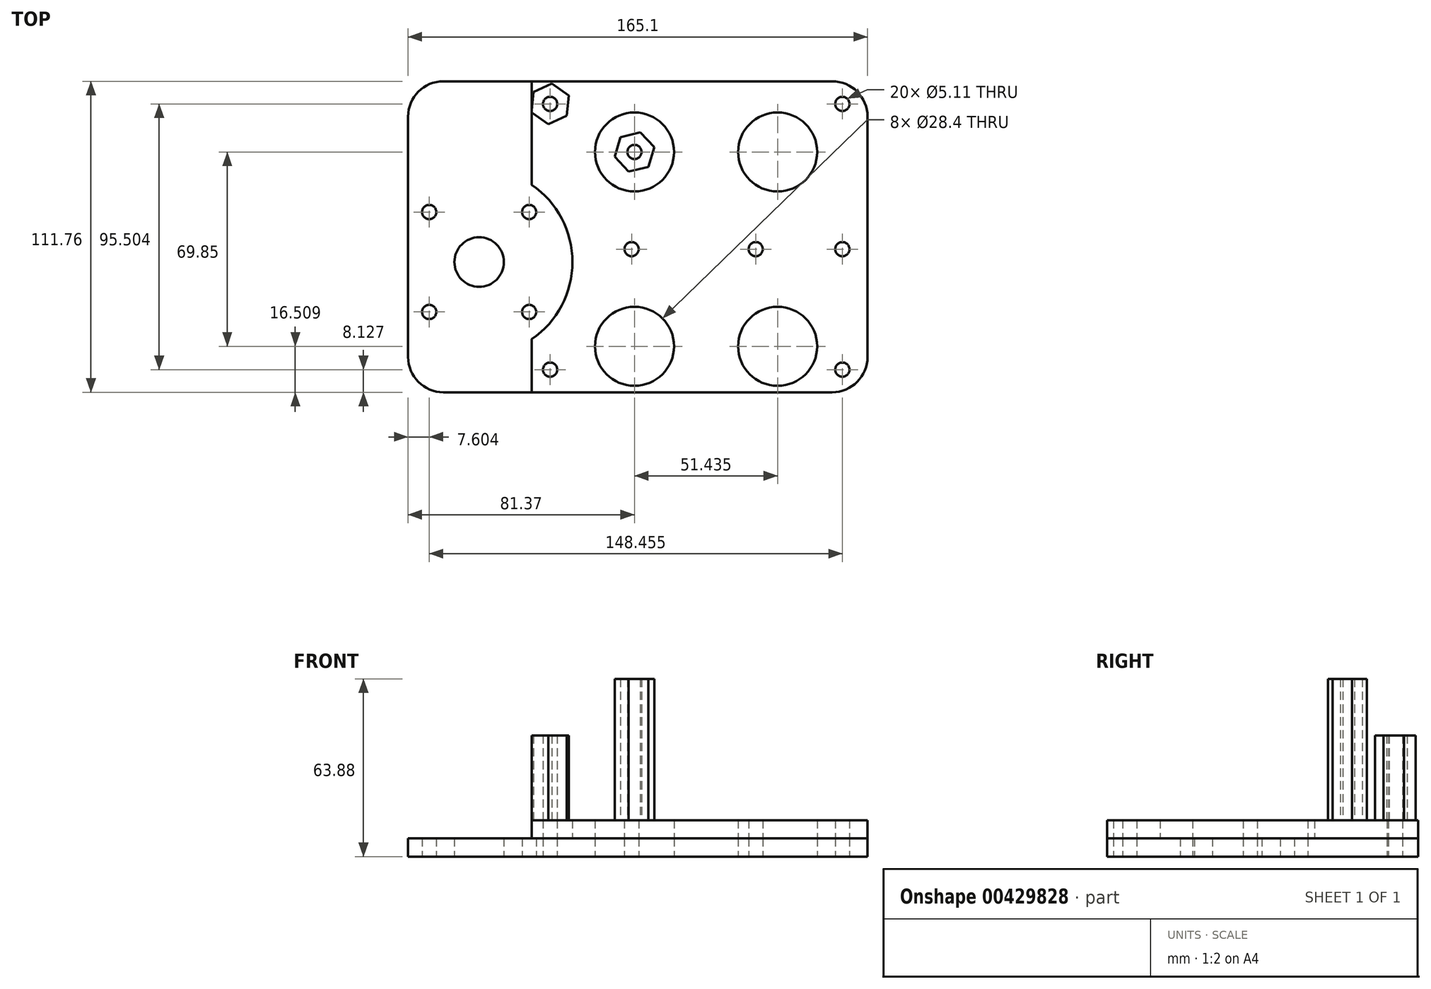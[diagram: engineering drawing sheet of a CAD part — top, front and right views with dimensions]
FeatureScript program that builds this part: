
annotation { "Feature Type Name" : "Feature", "Feature Type Description" : "" }
export const myFeature = defineFeature(function(context is Context, id is Id, definition is map)
    precondition{}
    {
        {
            var Q0;
            Q0=qCreatedBy(makeId("Top.planeOp"),FACE);
            var sketch = newSketch(context, id + "F0", { "sketchPlane" : qUnion([Q0])});
            skLineSegment(sketch, "E0.bottom", {"start": v(-81.37, 110.22) * mm, "end": v(83.73, 110.22) * mm});
            skLineSegment(sketch, "E0.top", {"start": v(-81.37, -1.54) * mm, "end": v(83.73, -1.54) * mm});
            skLineSegment(sketch, "E0.left", {"start": v(-81.37, 110.22) * mm, "end": v(-81.37, -1.54) * mm});
            skLineSegment(sketch, "E0.right", {"start": v(83.73, 110.22) * mm, "end": v(83.73, -1.54) * mm});
            skPoint(sketch, "E0.middle", {"position": v(1.18, 54.34) * mm});
            skLineSegment(sketch, "E1", {"start": v(25.72, 110.22) * mm, "end": v(25.72, -1.54) * mm, "construction": true});
            skCircle(sketch, "E2", {"center": v(0, 84.82) * mm, "radius": 14.2 * mm});
            skCircle(sketch, "E3", {"center": v(51.44, 84.82) * mm, "radius": 14.2 * mm});
            skLineSegment(sketch, "E4.trimOffspring", {"start": v(0, 84.82) * mm, "end": v(51.44, 84.82) * mm, "construction": true});
            skPoint(sketch, "E5.trimOffspring.end.orphan", {"position": v(83.73, 92.44) * mm});
            skPoint(sketch, "E6", {"position": v(25.72, 84.82) * mm});
            skCircle(sketch, "E7", {"center": v(0, 84.82) * mm, "radius": 25.4 * mm, "construction": true});
            skCircle(sketch, "E8", {"center": v(51.44, 84.82) * mm, "radius": 25.4 * mm, "construction": true});
            skLineSegment(sketch, "E9", {"start": v(-21.94, 49.9) * mm, "end": v(65.42, 49.9) * mm, "construction": true});
            skCircle(sketch, "E10.MirrorC", {"center": v(0, 14.97) * mm, "radius": 25.4 * mm, "construction": true});
            skCircle(sketch, "E11.MirrorC", {"center": v(0, 14.97) * mm, "radius": 14.2 * mm});
            skCircle(sketch, "E12.MirrorC", {"center": v(51.44, 14.97) * mm, "radius": 14.2 * mm});
            skCircle(sketch, "E13.MirrorC", {"center": v(51.44, 14.97) * mm, "radius": 25.4 * mm, "construction": true});
            skLineSegment(sketch, "E14.bottom", {"start": v(-73.77, 63.23) * mm, "end": v(-37.85, 63.23) * mm, "construction": true});
            skLineSegment(sketch, "E14.top", {"start": v(-73.77, 27.3) * mm, "end": v(-37.85, 27.3) * mm, "construction": true});
            skLineSegment(sketch, "E14.left", {"start": v(-73.77, 63.23) * mm, "end": v(-73.77, 27.3) * mm, "construction": true});
            skLineSegment(sketch, "E14.right", {"start": v(-37.85, 63.23) * mm, "end": v(-37.85, 27.3) * mm, "construction": true});
            skPoint(sketch, "E14.middle", {"position": v(-55.8, 45.27) * mm});
            skCircle(sketch, "E15", {"center": v(-55.8, 45.27) * mm, "radius": 8.9 * mm});
            skCircle(sketch, "E16", {"center": v(-73.77, 63.23) * mm, "radius": 2.55 * mm});
            skCircle(sketch, "E17", {"center": v(-37.85, 63.23) * mm, "radius": 2.55 * mm});
            skCircle(sketch, "E18", {"center": v(-37.85, 27.3) * mm, "radius": 2.55 * mm});
            skCircle(sketch, "E19", {"center": v(-73.77, 27.3) * mm, "radius": 2.55 * mm});
            skCircle(sketch, "E20", {"center": v(-55.8, 45.27) * mm, "radius": 25.4 * mm, "construction": true});
            skCircle(sketch, "E21", {"center": v(-1.05, 49.9) * mm, "radius": 2.55 * mm});
            skCircle(sketch, "E22", {"center": v(43.56, 49.9) * mm, "radius": 2.55 * mm});
            skCircle(sketch, "E23", {"center": v(74.69, 49.9) * mm, "radius": 2.55 * mm});
            skCircle(sketch, "E24", {"center": v(74.69, 6.59) * mm, "radius": 2.55 * mm});
            skCircle(sketch, "E25", {"center": v(74.69, 102.1) * mm, "radius": 2.55 * mm});
            skCircle(sketch, "E26", {"center": v(-30.32, 102.1) * mm, "radius": 2.55 * mm});
            skCircle(sketch, "E27", {"center": v(-30.32, 6.59) * mm, "radius": 2.55 * mm});
            skCircle(sketch, "E28", {"center": v(-30.32, 6.59) * mm, "radius": 6.88 * mm, "construction": true});
            skCircle(sketch, "E29", {"center": v(74.69, 6.59) * mm, "radius": 6.87 * mm, "construction": true});
            skLineSegment(sketch, "E30.bottom", {"start": v(-30.32, 102.1) * mm, "end": v(74.69, 102.1) * mm, "construction": true});
            skLineSegment(sketch, "E30.top", {"start": v(-30.32, 6.59) * mm, "end": v(74.69, 6.59) * mm, "construction": true});
            skLineSegment(sketch, "E30.left", {"start": v(-30.32, 102.1) * mm, "end": v(-30.32, 6.59) * mm, "construction": true});
            skLineSegment(sketch, "E30.right", {"start": v(74.69, 102.1) * mm, "end": v(74.69, 6.59) * mm, "construction": true});
            skSolve(sketch);
        }
        {
            var Q0;
            Q0=makeQuery(id+"F0.imprint","IMPRINT",FACE,{"disambiguationData":[TD([[makeQuery(id+"F0.imprint","IMPRINT",EDGE,{"derivedFrom":sQuery(id+"F0.wireOp",EDGE,"E0.bottom")}),-1.0]])]});
            extrude(context, id + "F1", {"entities" : qUnion([Q0]), "depth" : 6.6 * mm});
        }
        {
            var Q0;
            Q0=makeQuery(id+"F1.opExtrude","SWEPT_EDGE",EDGE,{"disambiguationData":[OSD([sQuery(id+"F0.wireOp",EDGE,"E0.bottom"),sQuery(id+"F0.wireOp",EDGE,"E0.left")])]});
            var Q1;
            Q1=makeQuery(id+"F1.opExtrude","SWEPT_EDGE",EDGE,{"disambiguationData":[OSD([sQuery(id+"F0.wireOp",EDGE,"E0.top"),sQuery(id+"F0.wireOp",EDGE,"E0.left")])]});
            var Q2;
            Q2=makeQuery(id+"F1.opExtrude","SWEPT_EDGE",EDGE,{"disambiguationData":[OSD([sQuery(id+"F0.wireOp",EDGE,"E0.top"),sQuery(id+"F0.wireOp",EDGE,"E0.right")])]});
            var Q3;
            Q3=makeQuery(id+"F1.opExtrude","SWEPT_EDGE",EDGE,{"disambiguationData":[OSD([sQuery(id+"F0.wireOp",EDGE,"E0.bottom"),sQuery(id+"F0.wireOp",EDGE,"E0.right")])]});
            fillet(context, id + "F2", {"entities" : qUnion([Q0, Q1, Q2, Q3]), "radius" : 12.7 * mm, "tangentPropagation" : true, "allowEdgeOverflow" : false});
        }
        {
            var Q0;
            Q0=makeQuery(id+"F1.opExtrude","CAP_FACE",FACE,{"disambiguationData":[OSD([sQuery(id+"F0.wireOp",EDGE,"E0.bottom"),sQuery(id+"F0.wireOp",EDGE,"E0.top"),sQuery(id+"F0.wireOp",EDGE,"E0.left"),sQuery(id+"F0.wireOp",EDGE,"E0.right"),sQuery(id+"F0.wireOp",EDGE,"E2"),sQuery(id+"F0.wireOp",EDGE,"E3"),sQuery(id+"F0.wireOp",EDGE,"E11.MirrorC"),sQuery(id+"F0.wireOp",EDGE,"E12.MirrorC"),sQuery(id+"F0.wireOp",EDGE,"E15"),sQuery(id+"F0.wireOp",EDGE,"E16"),sQuery(id+"F0.wireOp",EDGE,"E17"),sQuery(id+"F0.wireOp",EDGE,"E18"),sQuery(id+"F0.wireOp",EDGE,"E19"),sQuery(id+"F0.wireOp",EDGE,"E21"),sQuery(id+"F0.wireOp",EDGE,"E22"),sQuery(id+"F0.wireOp",EDGE,"E23"),sQuery(id+"F0.wireOp",EDGE,"E24"),sQuery(id+"F0.wireOp",EDGE,"E25"),sQuery(id+"F0.wireOp",EDGE,"E26"),sQuery(id+"F0.wireOp",EDGE,"E27")])],"isStart":false});
            var sketch = newSketch(context, id + "F3", { "sketchPlane" : qUnion([Q0])});
            skCircle(sketch, "E31.0", {"center": v(0, 84.82) * mm, "radius": 14.2 * mm});
            skCircle(sketch, "E32.0", {"center": v(-55.8, 45.27) * mm, "radius": 8.9 * mm});
            skCircle(sketch, "E33.0", {"center": v(0, 14.97) * mm, "radius": 14.2 * mm});
            skCircle(sketch, "E34.0", {"center": v(-30.32, 6.59) * mm, "radius": 2.55 * mm});
            skCircle(sketch, "E35.0", {"center": v(51.44, 14.97) * mm, "radius": 14.2 * mm});
            skCircle(sketch, "E36.0", {"center": v(51.44, 84.82) * mm, "radius": 14.2 * mm});
            skCircle(sketch, "E37.0", {"center": v(-30.32, 102.1) * mm, "radius": 2.55 * mm});
            skCircle(sketch, "E38.0", {"center": v(74.69, 102.1) * mm, "radius": 2.55 * mm});
            skCircle(sketch, "E39.0", {"center": v(74.69, 49.9) * mm, "radius": 2.55 * mm});
            skCircle(sketch, "E40.0", {"center": v(43.56, 49.9) * mm, "radius": 2.55 * mm});
            skCircle(sketch, "E41.0", {"center": v(-1.05, 49.9) * mm, "radius": 2.55 * mm});
            skCircle(sketch, "E42.0", {"center": v(-37.85, 27.3) * mm, "radius": 2.55 * mm});
            skCircle(sketch, "E43.0", {"center": v(-37.85, 63.23) * mm, "radius": 2.55 * mm});
            skCircle(sketch, "E44.0", {"center": v(-73.77, 27.3) * mm, "radius": 2.55 * mm});
            skCircle(sketch, "E45.0", {"center": v(-73.77, 63.23) * mm, "radius": 2.55 * mm});
            skLineSegment(sketch, "E46.0", {"start": v(-68.67, 110.22) * mm, "end": v(71.03, 110.22) * mm});
            skArc(sketch, "E47.0", {"start": v(-68.67, 110.22) * mm, "mid": v(-77.65, 106.5) * mm, "end": v(-81.37, 97.52) * mm});
            skLineSegment(sketch, "E48.0", {"start": v(-68.67, -1.54) * mm, "end": v(71.03, -1.54) * mm});
            skLineSegment(sketch, "E49.0", {"start": v(-81.37, 97.52) * mm, "end": v(-81.37, 11.16) * mm});
            skArc(sketch, "E50.0", {"start": v(-81.37, 11.16) * mm, "mid": v(-77.65, 2.18) * mm, "end": v(-68.67, -1.54) * mm});
            skArc(sketch, "E51.0", {"start": v(71.03, -1.54) * mm, "mid": v(80.01, 2.18) * mm, "end": v(83.73, 11.16) * mm});
            skLineSegment(sketch, "E52.0", {"start": v(83.73, 97.52) * mm, "end": v(83.73, 11.16) * mm});
            skArc(sketch, "E53.0", {"start": v(83.73, 97.52) * mm, "mid": v(80.01, 106.5) * mm, "end": v(71.03, 110.22) * mm});
            skArc(sketch, "E54", {"start": v(-36.92, 17.57) * mm, "mid": v(-22.28, 45.27) * mm, "end": v(-36.92, 72.97) * mm});
            skLineSegment(sketch, "E55", {"start": v(-36.92, 110.22) * mm, "end": v(-36.92, 72.97) * mm});
            skLineSegment(sketch, "E56.trimOffspring", {"start": v(-36.92, 17.57) * mm, "end": v(-36.92, -1.54) * mm});
            skSolve(sketch);
        }
        {
            var Q0;
            Q0=makeQuery(id+"F3.imprint","IMPRINT",FACE,{"disambiguationData":[TD([[makeQuery(id+"F3.imprint","IMPRINT",EDGE,{"derivedFrom":sQuery(id+"F3.wireOp",EDGE,"E31.0")}),-1.0]])]});
            extrude(context, id + "F4", {"entities" : qUnion([Q0]), "depth" : 6.48 * mm});
        }
        {
            var Q0;
            Q0=makeQuery(id+"F4.opExtrude","CAP_FACE",FACE,{"disambiguationData":[OSD([sQuery(id+"F0.wireOp",EDGE,"E24"),sQuery(id+"F3.wireOp",EDGE,"E31.0"),sQuery(id+"F3.wireOp",EDGE,"E33.0"),sQuery(id+"F3.wireOp",EDGE,"E34.0"),sQuery(id+"F3.wireOp",EDGE,"E35.0"),sQuery(id+"F3.wireOp",EDGE,"E36.0"),sQuery(id+"F3.wireOp",EDGE,"E37.0"),sQuery(id+"F3.wireOp",EDGE,"E38.0"),sQuery(id+"F3.wireOp",EDGE,"E39.0"),sQuery(id+"F3.wireOp",EDGE,"E40.0"),sQuery(id+"F3.wireOp",EDGE,"E41.0"),sQuery(id+"F3.wireOp",EDGE,"E46.0"),sQuery(id+"F3.wireOp",EDGE,"E48.0"),sQuery(id+"F3.wireOp",EDGE,"E51.0"),sQuery(id+"F3.wireOp",EDGE,"E52.0"),sQuery(id+"F3.wireOp",EDGE,"E53.0"),sQuery(id+"F3.wireOp",EDGE,"E54"),sQuery(id+"F3.wireOp",EDGE,"E55"),sQuery(id+"F3.wireOp",EDGE,"E56.trimOffspring")])],"isStart":false});
            var sketch = newSketch(context, id + "F5", { "sketchPlane" : qUnion([Q0])});
            skCircle(sketch, "E57.0", {"center": v(-30.32, 102.1) * mm, "radius": 2.55 * mm});
            skCircle(sketch, "E58.cCircle", {"center": v(-30.32, 102.1) * mm, "radius": 7.33 * mm, "construction": true});
            skLineSegment(sketch, "E58.0", {"start": v(-24.34, 97.85) * mm, "end": v(-31, 94.8) * mm});
            skLineSegment(sketch, "E58.1", {"start": v(-31, 94.8) * mm, "end": v(-36.98, 99.04) * mm});
            skLineSegment(sketch, "E58.2", {"start": v(-36.98, 99.04) * mm, "end": v(-36.3, 106.34) * mm});
            skLineSegment(sketch, "E58.3", {"start": v(-36.3, 106.34) * mm, "end": v(-29.63, 109.4) * mm});
            skLineSegment(sketch, "E58.4", {"start": v(-29.63, 109.4) * mm, "end": v(-23.65, 105.15) * mm});
            skLineSegment(sketch, "E58.5", {"start": v(-23.65, 105.15) * mm, "end": v(-24.34, 97.85) * mm});
            skSolve(sketch);
        }
        {
            var Q0;
            Q0=makeQuery(id+"F5.imprint","IMPRINT",FACE,{"disambiguationData":[TD([[makeQuery(id+"F5.imprint","IMPRINT",EDGE,{"derivedFrom":sQuery(id+"F5.wireOp",EDGE,"E57.0")}),-1.0]])]});
            extrude(context, id + "F6", {"entities" : qUnion([Q0]), "depth" : 30.48 * mm});
        }
        {
            var Q0;
            Q0=makeQuery(id+"F4.opExtrude","CAP_FACE",FACE,{"disambiguationData":[OSD([sQuery(id+"F0.wireOp",EDGE,"E24"),sQuery(id+"F3.wireOp",EDGE,"E31.0"),sQuery(id+"F3.wireOp",EDGE,"E33.0"),sQuery(id+"F3.wireOp",EDGE,"E34.0"),sQuery(id+"F3.wireOp",EDGE,"E35.0"),sQuery(id+"F3.wireOp",EDGE,"E36.0"),sQuery(id+"F3.wireOp",EDGE,"E37.0"),sQuery(id+"F3.wireOp",EDGE,"E38.0"),sQuery(id+"F3.wireOp",EDGE,"E39.0"),sQuery(id+"F3.wireOp",EDGE,"E40.0"),sQuery(id+"F3.wireOp",EDGE,"E41.0"),sQuery(id+"F3.wireOp",EDGE,"E46.0"),sQuery(id+"F3.wireOp",EDGE,"E48.0"),sQuery(id+"F3.wireOp",EDGE,"E51.0"),sQuery(id+"F3.wireOp",EDGE,"E52.0"),sQuery(id+"F3.wireOp",EDGE,"E53.0"),sQuery(id+"F3.wireOp",EDGE,"E54"),sQuery(id+"F3.wireOp",EDGE,"E55"),sQuery(id+"F3.wireOp",EDGE,"E56.trimOffspring")])],"isStart":false});
            var sketch = newSketch(context, id + "F7", { "sketchPlane" : qUnion([Q0])});
            skCircle(sketch, "E59.0", {"center": v(0, 84.82) * mm, "radius": 14.2 * mm});
            skCircle(sketch, "E60", {"center": v(0, 84.82) * mm, "radius": 2.55 * mm});
            skCircle(sketch, "E61.cCircle", {"center": v(0, 84.82) * mm, "radius": 7.33 * mm, "construction": true});
            skLineSegment(sketch, "E61.0", {"start": v(5.02, 79.48) * mm, "end": v(-2.12, 77.8) * mm});
            skLineSegment(sketch, "E61.1", {"start": v(-2.12, 77.8) * mm, "end": v(-7.14, 83.14) * mm});
            skLineSegment(sketch, "E61.2", {"start": v(-7.14, 83.14) * mm, "end": v(-5.02, 90.16) * mm});
            skLineSegment(sketch, "E61.3", {"start": v(-5.02, 90.16) * mm, "end": v(2.12, 91.84) * mm});
            skLineSegment(sketch, "E61.4", {"start": v(2.12, 91.84) * mm, "end": v(7.14, 86.5) * mm});
            skLineSegment(sketch, "E61.5", {"start": v(7.14, 86.5) * mm, "end": v(5.02, 79.48) * mm});
            skSolve(sketch);
        }
        {
            var Q0;
            Q0=makeQuery(id+"F7.imprint","IMPRINT",FACE,{"disambiguationData":[TD([[makeQuery(id+"F7.imprint","IMPRINT",EDGE,{"derivedFrom":sQuery(id+"F7.wireOp",EDGE,"E60")}),-1.0]])]});
            extrude(context, id + "F8", {"entities" : qUnion([Q0]), "depth" : 50.8 * mm});
        }
    });
